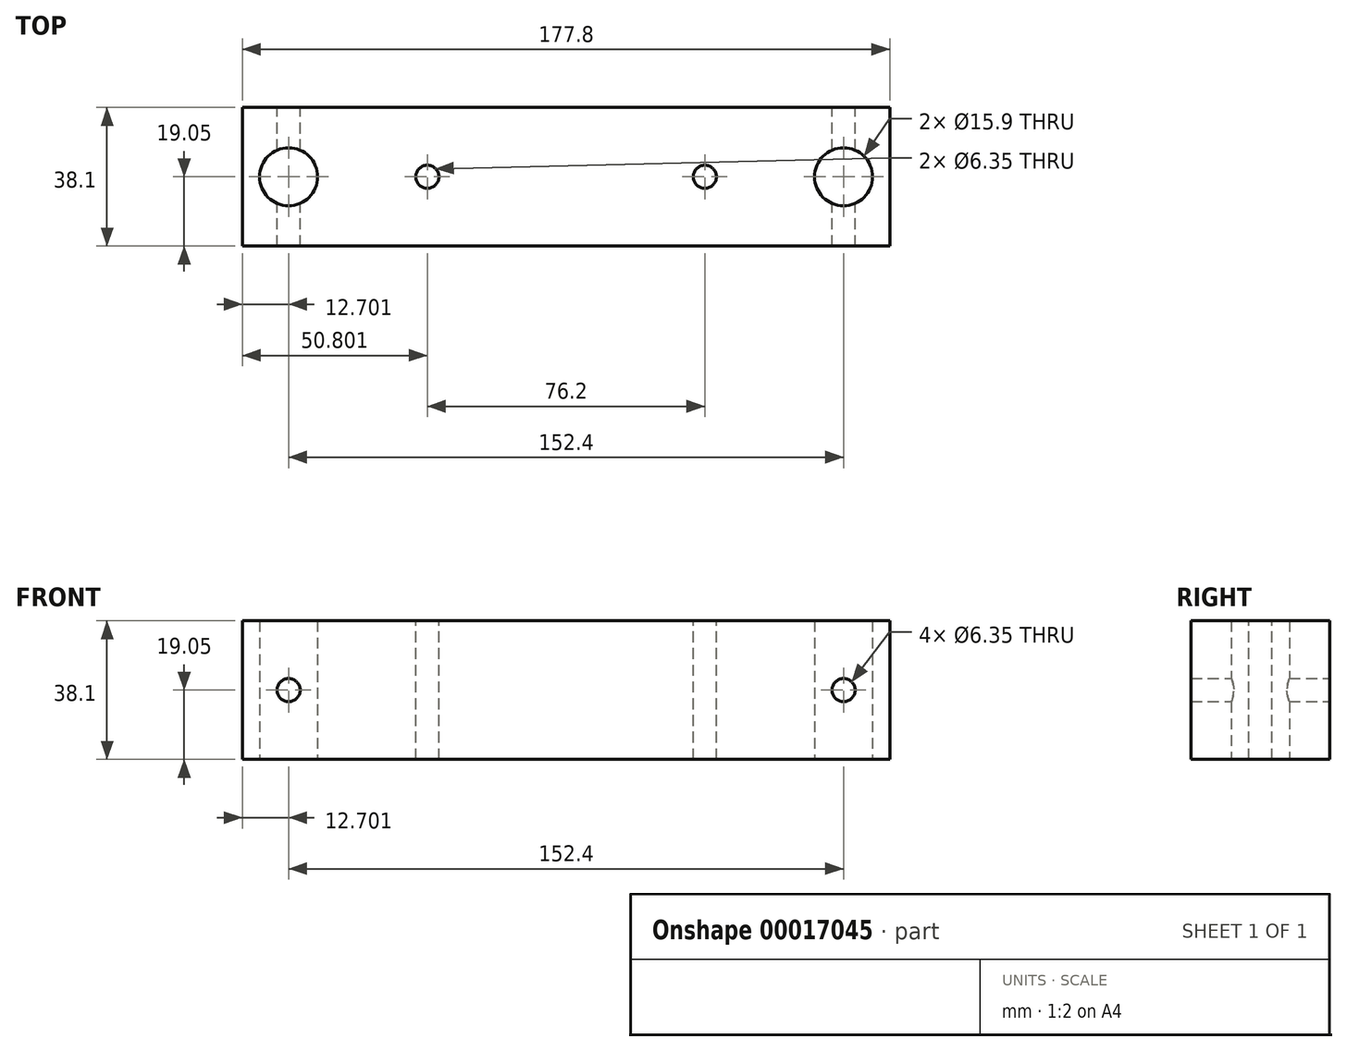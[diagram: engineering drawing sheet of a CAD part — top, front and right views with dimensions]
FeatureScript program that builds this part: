
annotation { "Feature Type Name" : "Feature", "Feature Type Description" : "" }
export const myFeature = defineFeature(function(context is Context, id is Id, definition is map)
    precondition{}
    {
        {
            var Q0;
            Q0=qCreatedBy(makeId("Top.planeOp"),FACE);
            var sketch = newSketch(context, id + "F0", { "sketchPlane" : qUnion([Q0])});
            skCircle(sketch, "E0", {"center": v(-67.59, 0) * mm, "radius": 7.95 * mm});
            skCircle(sketch, "E1", {"center": v(84.81, 0) * mm, "radius": 7.95 * mm});
            skLineSegment(sketch, "E2.rect.bottom", {"start": v(97.51, 19.05) * mm, "end": v(-80.29, 19.05) * mm});
            skLineSegment(sketch, "E2.rect.top", {"start": v(97.51, -19.05) * mm, "end": v(-80.29, -19.05) * mm});
            skLineSegment(sketch, "E2.rect.left", {"start": v(97.51, 19.05) * mm, "end": v(97.51, -19.05) * mm});
            skLineSegment(sketch, "E2.rect.right", {"start": v(-80.29, 19.05) * mm, "end": v(-80.29, -19.05) * mm});
            skPoint(sketch, "E2.rect.middle", {"position": v(8.61, 0) * mm});
            skSolve(sketch);
        }
        {
            var Q0;
            Q0 = qSketchRegion(id + "F0", true);
            extrude(context, id + "F1", {"entities" : qUnion([Q0]), "depth" : 38.1 * mm});
        }
        {
            var Q0;
            Q0=makeQuery(id+"F1.opExtrude","SWEPT_FACE",FACE,{"disambiguationData":[OSD([sQuery(id+"F0.wireOp",EDGE,"E2.rect.bottom")])]});
            var sketch = newSketch(context, id + "F2", { "sketchPlane" : qUnion([Q0])});
            skCircle(sketch, "E3", {"center": v(-84.81, 19.05) * mm, "radius": 3.18 * mm});
            skCircle(sketch, "E4", {"center": v(67.59, 19.05) * mm, "radius": 3.18 * mm});
            skSolve(sketch);
        }
        {
            var Q0;
            Q0 = qSketchRegion(id + "F2", true);
            extrude(context, id + "F3", {"entities" : qUnion([Q0]), "operationType" : NewBodyOperationType.REMOVE, "oppositeDirection" : true, "depth" : 78.6 * mm});
        }
        {
            var Q0;
            Q0=makeQuery(id+"F1.opExtrude","CAP_FACE",FACE,{"disambiguationData":[OSD([sQuery(id+"F0.wireOp",EDGE,"E0"),sQuery(id+"F0.wireOp",EDGE,"E1"),sQuery(id+"F0.wireOp",EDGE,"E2.rect.bottom"),sQuery(id+"F0.wireOp",EDGE,"E2.rect.top"),sQuery(id+"F0.wireOp",EDGE,"E2.rect.left"),sQuery(id+"F0.wireOp",EDGE,"E2.rect.right")])],"isStart":false});
            var sketch = newSketch(context, id + "F4", { "sketchPlane" : qUnion([Q0])});
            skLineSegment(sketch, "E5", {"start": v(8.61, 19.05) * mm, "end": v(8.61, -19.05) * mm});
            skCircle(sketch, "E6", {"center": v(46.71, 0) * mm, "radius": 3.18 * mm});
            skPoint(sketch, "E6.centerSnap0", {"position": v(8.61, 0) * mm});
            skCircle(sketch, "E7", {"center": v(-29.49, 0) * mm, "radius": 3.18 * mm});
            skSolve(sketch);
        }
        {
            var Q0;
            Q0 = qSketchRegion(id + "F4", true);
            extrude(context, id + "F5", {"entities" : qUnion([Q0]), "operationType" : NewBodyOperationType.REMOVE, "endBound" : BoundingType.THROUGH_ALL, "oppositeDirection" : true, "depth" : 25.4 * mm});
        }
    });
